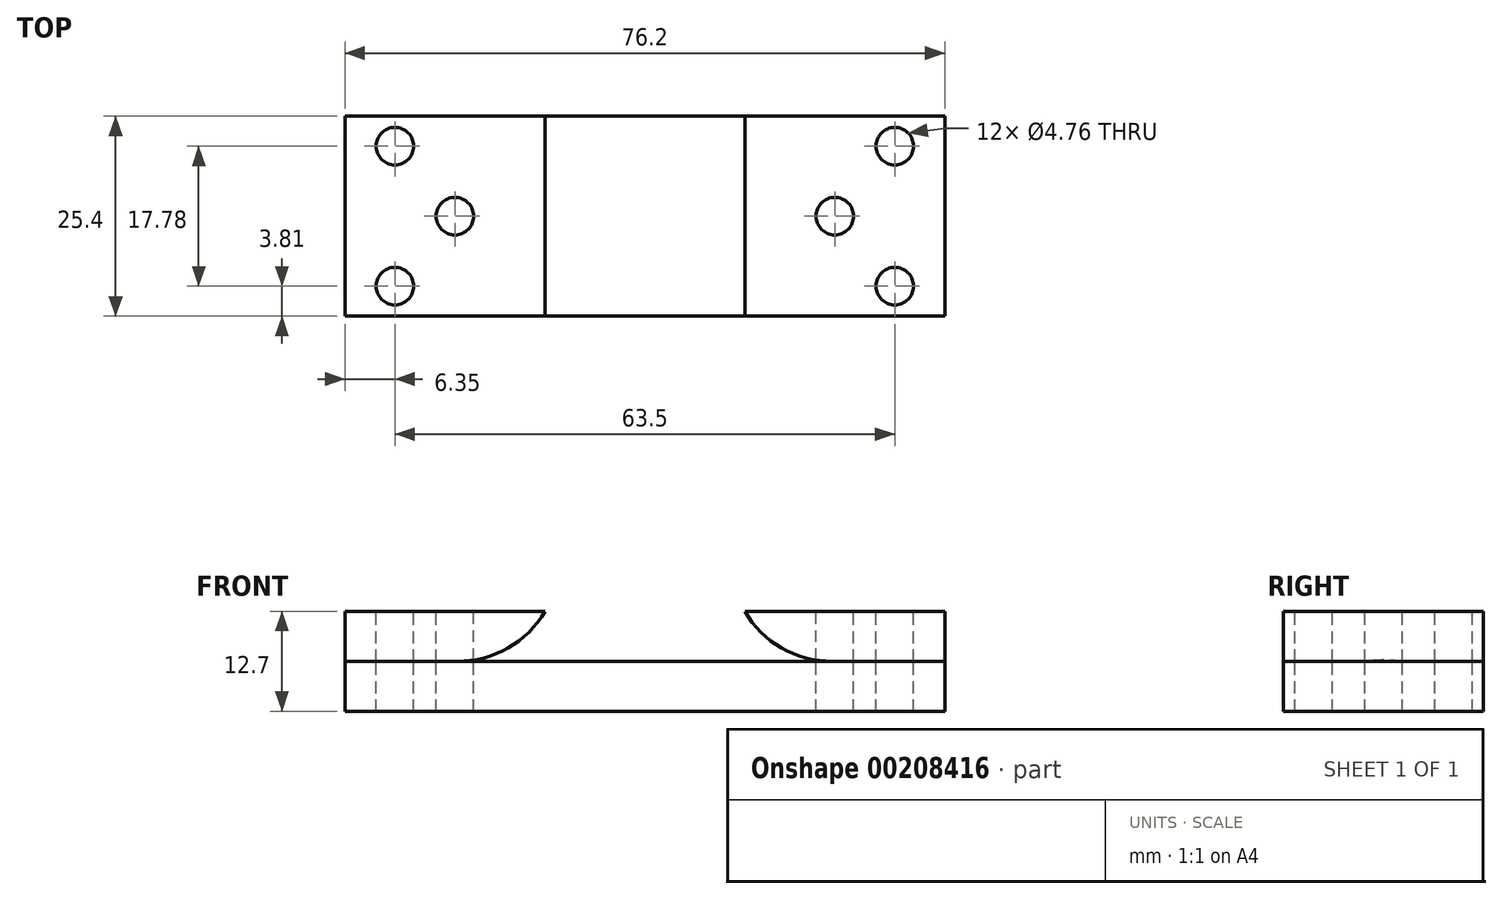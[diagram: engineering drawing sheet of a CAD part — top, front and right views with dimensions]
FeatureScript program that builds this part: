
annotation { "Feature Type Name" : "Feature", "Feature Type Description" : "" }
export const myFeature = defineFeature(function(context is Context, id is Id, definition is map)
    precondition{}
    {
        {
            var Q0;
            Q0=qCreatedBy(makeId("Front.planeOp"),FACE);
            var sketch = newSketch(context, id + "F0", { "sketchPlane" : qUnion([Q0])});
            skLineSegment(sketch, "E0.bottom", {"start": v(0, 0) * mm, "end": v(31.75, 0) * mm});
            skLineSegment(sketch, "E0.top", {"start": v(0, 6.35) * mm, "end": v(25.4, 6.35) * mm});
            skLineSegment(sketch, "E0.left", {"start": v(0, 0) * mm, "end": v(0, 6.35) * mm});
            skLineSegment(sketch, "E1", {"start": v(31.75, 0) * mm, "end": v(25.4, 6.35) * mm});
            skSolve(sketch);
        }
        {
            var Q0;
            Q0=makeQuery(id+"F0.imprint","IMPRINT",FACE,{"disambiguationData":[TD([[makeQuery(id+"F0.imprint","IMPRINT",EDGE,{"derivedFrom":sQuery(id+"F0.wireOp",EDGE,"E0.bottom")}),1.0]])]});
            extrude(context, id + "F1", {"entities" : qUnion([Q0]), "depth" : 25.4 * mm});
        }
        {
            var Q0;
            Q0=makeQuery(id+"F1.opExtrude","SWEPT_FACE",FACE,{"disambiguationData":[OSD([sQuery(id+"F0.wireOp",EDGE,"E0.top")])]});
            var sketch = newSketch(context, id + "F2", { "sketchPlane" : qUnion([Q0])});
            skCircle(sketch, "E2", {"center": v(6.35, -3.81) * mm, "radius": 2.38 * mm});
            skCircle(sketch, "E3", {"center": v(6.35, -21.59) * mm, "radius": 2.38 * mm});
            skLineSegment(sketch, "E4", {"start": v(6.35, -3.8) * mm, "end": v(6.35, -21.59) * mm, "construction": true});
            skLineSegment(sketch, "E5", {"start": v(6.35, -12.7) * mm, "end": v(13.97, -12.7) * mm, "construction": true});
            skCircle(sketch, "E6", {"center": v(13.97, -12.7) * mm, "radius": 2.38 * mm});
            skSolve(sketch);
        }
        {
            var Q0;
            Q0=makeQuery(id+"F2.imprint","IMPRINT",FACE,{"disambiguationData":[TD([[makeQuery(id+"F2.imprint","IMPRINT",EDGE,{"derivedFrom":sQuery(id+"F2.wireOp",EDGE,"E3")}),1.0]])]});
            var Q1;
            Q1=makeQuery(id+"F2.imprint","IMPRINT",FACE,{"disambiguationData":[TD([[makeQuery(id+"F2.imprint","IMPRINT",EDGE,{"derivedFrom":sQuery(id+"F2.wireOp",EDGE,"E2")}),1.0]])]});
            var Q2;
            Q2=makeQuery(id+"F2.imprint","IMPRINT",FACE,{"disambiguationData":[TD([[makeQuery(id+"F2.imprint","IMPRINT",EDGE,{"derivedFrom":sQuery(id+"F2.wireOp",EDGE,"E6")}),1.0]])]});
            extrude(context, id + "F3", {"entities" : qUnion([Q0, Q1, Q2]), "operationType" : NewBodyOperationType.REMOVE, "endBound" : BoundingType.UP_TO_NEXT, "oppositeDirection" : true, "depth" : 9.52 * mm});
        }
        {
            var Q0;
            Q0=makeQuery(id+"F1.opExtrude","SWEPT_FACE",FACE,{"disambiguationData":[OSD([sQuery(id+"F0.wireOp",EDGE,"E0.bottom")])]});
            var sketch = newSketch(context, id + "F4", { "sketchPlane" : qUnion([Q0])});
            skCircle(sketch, "E7.0", {"center": v(6.35, 21.59) * mm, "radius": 2.38 * mm});
            skCircle(sketch, "E7.1", {"center": v(13.97, 12.7) * mm, "radius": 2.38 * mm});
            skCircle(sketch, "E7.2", {"center": v(6.35, 3.81) * mm, "radius": 2.38 * mm});
            skLineSegment(sketch, "E8.bottom", {"start": v(0, 0) * mm, "end": v(76.2, 0) * mm});
            skLineSegment(sketch, "E8.top", {"start": v(0, 25.4) * mm, "end": v(76.2, 25.4) * mm});
            skLineSegment(sketch, "E8.left", {"start": v(0, 0) * mm, "end": v(0, 25.4) * mm});
            skLineSegment(sketch, "E8.right", {"start": v(76.2, 0) * mm, "end": v(76.2, 25.4) * mm});
            skLineSegment(sketch, "E9", {"start": v(38.1, 25.4) * mm, "end": v(38.1, 0) * mm, "construction": true});
            skCircle(sketch, "E10.MirrorC", {"center": v(69.85, 3.81) * mm, "radius": 2.38 * mm});
            skCircle(sketch, "E11.MirrorC", {"center": v(62.23, 12.7) * mm, "radius": 2.38 * mm});
            skCircle(sketch, "E12.MirrorC", {"center": v(69.85, 21.59) * mm, "radius": 2.38 * mm});
            skSolve(sketch);
        }
        {
            var Q0;
            Q0 = qSketchRegion(id + "F4", true);
            extrude(context, id + "F5", {"entities" : qUnion([Q0]), "depth" : 6.35 * mm});
        }
        {
            var Q0;
            Q0=makeQuery(id+"F1.opExtrude","SWEPT_BODY",BODY,{"disambiguationData":[OSD([sQuery(id+"F0.wireOp",EDGE,"E0.bottom"),sQuery(id+"F0.wireOp",EDGE,"E0.top"),sQuery(id+"F0.wireOp",EDGE,"E0.left"),sQuery(id+"F0.wireOp",EDGE,"E1")])]});
            var Q1;
            Q1=makeQuery(id+"F1.opExtrude","CAP_EDGE",EDGE,{"disambiguationData":[OSD([sQuery(id+"F0.wireOp",EDGE,"E0.left")])],"isStart":false});
            transform(context, id + "F6", {"entities" : qUnion([Q0]), "transformType" : TransformType.ROTATION, "transformAxis" : qUnion([Q1]), "angle" : 180 * degree, "makeCopy" : true});
        }
        {
            var Q0;
            Q0=makeQuery(id+"F6.opPattern","COPY",BODY,{"derivedFrom":makeQuery(id+"F1.opExtrude","SWEPT_BODY",BODY,{"disambiguationData":[OSD([sQuery(id+"F0.wireOp",EDGE,"E0.bottom"),sQuery(id+"F0.wireOp",EDGE,"E0.top"),sQuery(id+"F0.wireOp",EDGE,"E0.left"),sQuery(id+"F0.wireOp",EDGE,"E1")])]}),"instanceName":"1"});
            var Q1;
            Q1=makeQuery(id+"F5.opExtrude","CAP_VERTEX",VERTEX,{"disambiguationData":[OSD([sQuery(id+"F4.wireOp",EDGE,"E8.top"),sQuery(id+"F4.wireOp",EDGE,"E8.left")])],"isStart":true});
            var Q2;
            Q2=makeQuery(id+"F5.opExtrude","CAP_VERTEX",VERTEX,{"disambiguationData":[OSD([sQuery(id+"F4.wireOp",EDGE,"E8.bottom"),sQuery(id+"F4.wireOp",EDGE,"E8.right")])],"isStart":true});
            transform(context, id + "F7", {"entities" : qUnion([Q0]), "transformType" : TransformType.TRANSLATION_ENTITY, "oppositeDirectionEntity" : false, "transformLine" : qUnion([Q1, Q2]), "makeCopy" : false});
        }
        {
            var Q0;
            Q0=makeQuery(id+"F1.opExtrude","SWEPT_EDGE",EDGE,{"disambiguationData":[OSD([sQuery(id+"F0.wireOp",EDGE,"E0.bottom"),sQuery(id+"F0.wireOp",EDGE,"E1")])]});
            var Q1;
            Q1=makeQuery(id+"F6.opPattern","COPY",EDGE,{"derivedFrom":makeQuery(id+"F1.opExtrude","SWEPT_EDGE",EDGE,{"disambiguationData":[OSD([sQuery(id+"F0.wireOp",EDGE,"E0.bottom"),sQuery(id+"F0.wireOp",EDGE,"E1")])]}),"instanceName":"1"});
            fillet(context, id + "F8", {"entities" : qUnion([Q0, Q1]), "radius" : 12.7 * mm, "tangentPropagation" : true, "allowEdgeOverflow" : false});
        }
    });
